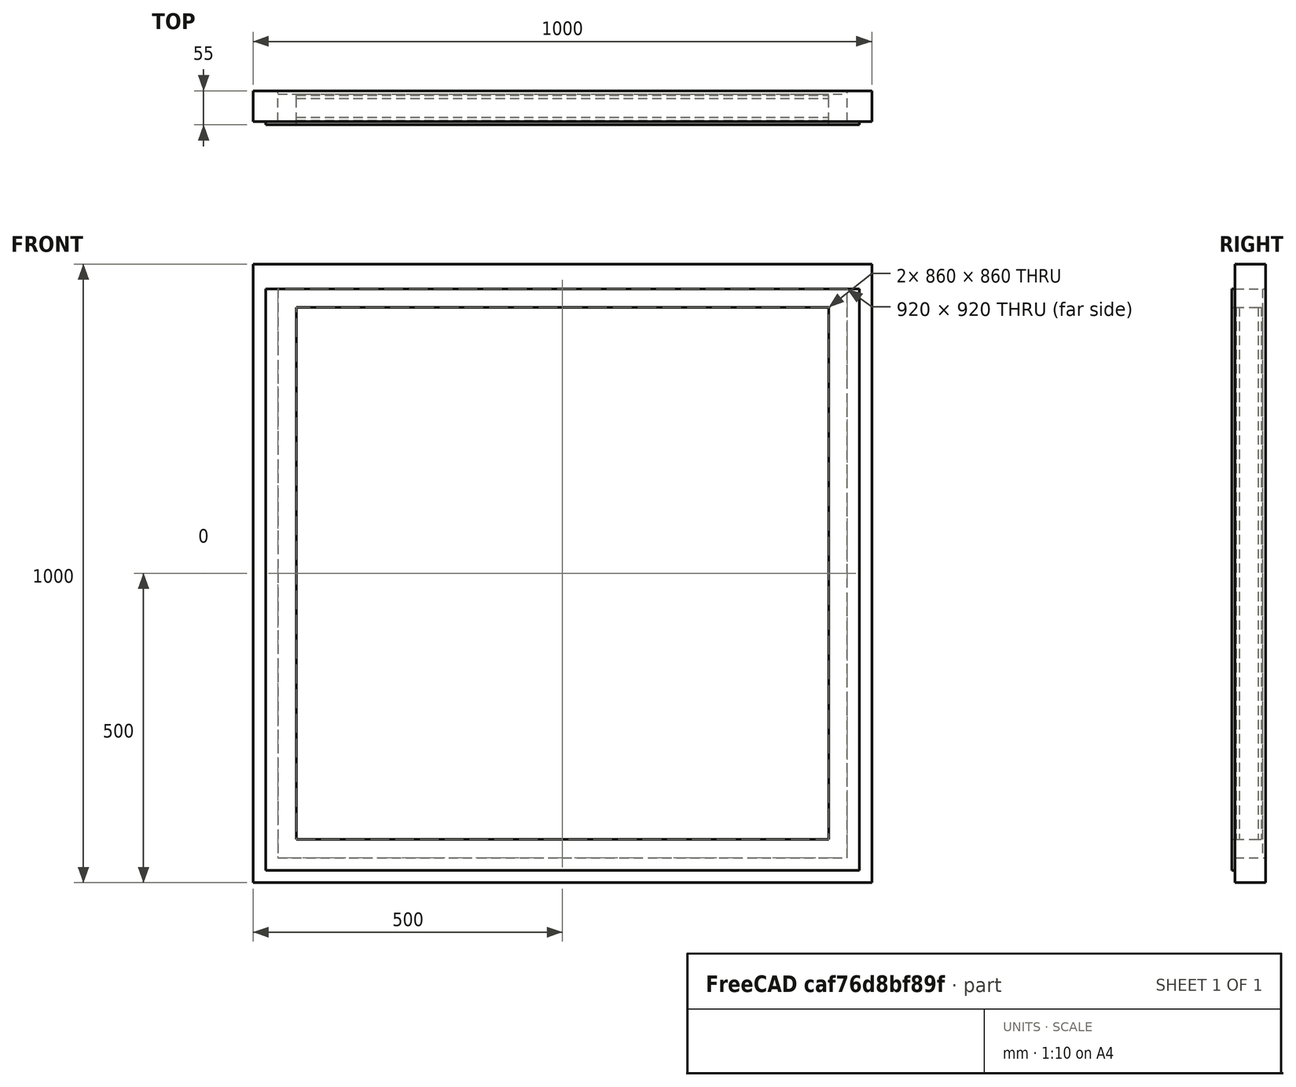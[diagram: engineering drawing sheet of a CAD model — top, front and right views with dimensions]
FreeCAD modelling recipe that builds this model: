
FCSTD DOCUMENT  (FreeCAD 0.16R6704 (Git))
Label: Maxim Air with double glazing and blind
License: CreativeCommons Attribution
LicenseURL: http://creativecommons.org/licenses/by/4.0/
objects: Sketcher::SketchObject×3, Part::FeaturePython×2, Part::Extrusion×1, App::DocumentObjectGroup×1
note: 6 computed .brp shape members not serialized (recipe doc carries the construction recipe); baked Part::Feature solids carry a one-line shape summary decoded from their .brp

FEATURE [Sketcher::SketchObject] Sketch102  label="Esboco_persiana_interna_02"
  Placement = pos=(0,0,0) rot=(1,0,0;1.5708rad)
  sketch-geometry (16):
    g0: LineSegment StartX=0 StartY=0 StartZ=0 EndX=1000 EndY=0 EndZ=0
    g1: LineSegment StartX=1000 StartY=0 StartZ=0 EndX=1000 EndY=1000 EndZ=0
    g2: LineSegment StartX=1000 StartY=1000 StartZ=0 EndX=0 EndY=1000 EndZ=0
    g3: LineSegment StartX=0 StartY=1000 StartZ=0 EndX=0 EndY=0 EndZ=0
    g4: LineSegment StartX=40 StartY=40 StartZ=0 EndX=960 EndY=40 EndZ=0
    g5: LineSegment StartX=960 StartY=40 StartZ=0 EndX=960 EndY=960 EndZ=0
    g6: LineSegment StartX=960 StartY=960 StartZ=0 EndX=40 EndY=960 EndZ=0
    g7: LineSegment StartX=40 StartY=960 StartZ=0 EndX=40 EndY=40 EndZ=0
    g8: LineSegment StartX=70 StartY=930 StartZ=0 EndX=930 EndY=930 EndZ=0
    g9: LineSegment StartX=930 StartY=930 StartZ=0 EndX=930 EndY=70 EndZ=0
    g10: LineSegment StartX=930 StartY=70 StartZ=0 EndX=70 EndY=70 EndZ=0
    g11: LineSegment StartX=70 StartY=70 StartZ=0 EndX=70 EndY=930 EndZ=0
    g12: LineSegment StartX=20 StartY=960 StartZ=0 EndX=980 EndY=960 EndZ=0
    g13: LineSegment StartX=980 StartY=960 StartZ=0 EndX=980 EndY=20 EndZ=0
    g14: LineSegment StartX=980 StartY=20 StartZ=0 EndX=20 EndY=20 EndZ=0
    g15: LineSegment StartX=20 StartY=20 StartZ=0 EndX=20 EndY=960 EndZ=0
  constraints (47):
    c: Coincident(g0,g1)
    c: Coincident(g1,g2)
    c: Coincident(g2,g3)
    c: Coincident(g3,g0)
    c: Horizontal(g0)
    c: Horizontal(g2)
    c: Vertical(g1)
    c: Vertical(g3)
    c: Coincident(g4,g5)
    c: Coincident(g5,g6)
    c: Coincident(g6,g7)
    c: Coincident(g7,g4)
    c: Horizontal(g4)
    c: Horizontal(g6)
    c: Vertical(g5)
    c: Vertical(g7)
    c: DistanceX(g0) = 1000  'Largura_vao'
    c: DistanceX(g2,g6) = 40  'Montante_vertical_1'
    c: DistanceX(g4,g0) = 40  'Montante_vertical_2'
    c: DistanceY(g0,g4) = 40  'Montante_inferior_caixilho'
    c: Coincident(g0,g-1)
    c: DistanceY(g0,g1) = 1000  'Altura_vao'
    c: Coincident(g8,g9)
    c: Coincident(g9,g10)
    c: Coincident(g10,g11)
    c: Coincident(g11,g8)
    c: Horizontal(g8)
    c: Horizontal(g10)
    c: Vertical(g9)
    c: Vertical(g11)
    c: DistanceX(g6,g8) = 30  'Montante_vertical_1_janela'
    c: DistanceY(g8,g6) = 30  'Montante_superior_janela'
    c: DistanceX(g8,g5) = 30  'Montante_vertical_2_janela'
    c: DistanceY(g4,g9) = 30  'Montante_inferior_janela'
    c: Coincident(g12,g13)
    c: Coincident(g13,g14)
    c: Coincident(g14,g15)
    c: Coincident(g15,g12)
    c: Horizontal(g12)
    c: Horizontal(g14)
    c: Vertical(g13)
    c: Vertical(g15)
    c: DistanceX(g4,g13) = 20  'Arremate vertical 2 janela'
    c: DistanceY(g13,g4) = 20  'Arremate_inferior'
    c: DistanceX(g14,g4) = 20  'Arremate_vertical_1'
    c: DistanceY(g6,g12) = 0
    c: DistanceY(g5,g1) = 40  'Montante_superior'
FEATURE [Part::FeaturePython] Window077  label="Maxim Air with double glazing and blind"  # WARN: FeaturePython — macro-defined, semantics opaque (R4)
  Base = -> Sketch102
  Height = 0
  HoleDepth = 0
  MoveWithHost = true
  Normal = (0,1,0)
  Preset = 0
  Role = 0
  Width = 0
  WindowParts = CAIXILHO | Frame | Wire0,Wire1 | 50.0 | 0.0 | JANELA | Frame | Wire1,Wire2 | 45.0 | 0.0 | ARREMATE | Frame | Wire2,Wire3 | 5.0 | -5.0 | VIDRO 1 | Glass panel | Wire2 | 5.0 | 2.0 | VIDRO 2 | Glass panel | Wire2 | 5.0 | 37.5
FEATURE [Sketcher::SketchObject] Sketch103
  ExternalGeometry = -> [Window077]
  Placement = pos=(70,0,0) rot=(0.57735,0.57735,0.57735;2.0944rad)
  Support = -> Window077 [Face19]
  sketch-geometry (3):
    g0: LineSegment [constr] StartX=22.5 StartY=1251.7 StartZ=0 EndX=22.5 EndY=-119.798 EndZ=0
    g1: ArcOfCircle CenterX=22.5 CenterY=921 CenterZ=0 NormalX=0 NormalY=0 NormalZ=1 Radius=7 StartAngle=1.5708 EndAngle=4.71239
    g2: ArcOfCircle CenterX=22.5 CenterY=907 CenterZ=0 NormalX=0 NormalY=0 NormalZ=1 Radius=7 StartAngle=4.71239 EndAngle=7.85398
  constraints (12):
    c: PointOnObject(g1,g0)
    c: PointOnObject(g1,g0)
    c: PointOnObject(g2,g0)
    c: PointOnObject(g2,g0)
    c: DistanceY(g1,g1) = 14
    c: DistanceY(g2,g1) = 14
    c: Vertical(g0)
    c: PointOnObject(g1,g0)
    c: PointOnObject(g2,g0)
    c: Coincident(g2,g1)
    c: Symmetric(g-3,g-3,g0)
    c: DistanceY(g1,g-3) = 2
FEATURE [Part::Extrusion] Extrude_Sketch103  label="Módulo persiana "
  Base = -> Sketch103
  Dir = (860,0,0)
  Solid = true
  expr: Dir.x = Esboco_persiana_interna_02.Constraints.Largura_vao - Esboco_persiana_interna_02.Constraints.Montante_vertical_1 - Esboco_persiana_interna_02.Constraints.Montante_vertical_1_janela - Esboco_persiana_interna_02.Constraints.Montante_vertical_2_janela - Esboco_persiana_interna_02.Constraints.Montante_vertical_2
FEATURE [Sketcher::SketchObject] Sketch104  label="Opening indication"
  ExternalGeometry = -> [Window077]
  Placement = pos=(0,2,0) rot=(1,0,0;1.5708rad)
  Support = -> Window077 [Face35]
  sketch-geometry (3):
    g0: LineSegment StartX=70 StartY=930 StartZ=0 EndX=500 EndY=70 EndZ=0
    g1: LineSegment StartX=500 StartY=70 StartZ=0 EndX=930 EndY=930 EndZ=0
    g2: LineSegment [constr] StartX=500 StartY=1142.4 StartZ=0 EndX=500 EndY=-164.202 EndZ=0
  constraints (7):
    c: Coincident(g-5,g0)
    c: PointOnObject(g0,g-4)
    c: Coincident(g0,g1)
    c: Vertical(g2)
    c: PointOnObject(g0,g2)
    c: Symmetric(g-5,g-6,g2)
    c: Coincident(g1,g-6)
FEATURE [Part::FeaturePython] Array004  label="Internal blind"  # Draft array (typed FeaturePython)
  Angle = 360
  ArrayType = 0
  Axis = (0,0,1)
  Base = -> Extrude_Sketch103
  Center = (0,0,0)
  Fuse = false
  IntervalAxis = (0,0,0)
  IntervalX = (1,0,0)
  IntervalY = (0,1,0)
  IntervalZ = (0,0,-28)
  NumberPolar = 1
  NumberX = 1
  NumberY = 1
  NumberZ = 31
  expr: NumberZ = (Esboco_persiana_interna_02.Constraints.Altura_vao - Esboco_persiana_interna_02.Constraints.Montante_inferior_caixilho - Esboco_persiana_interna_02.Constraints.Montante_inferior_janela - Esboco_persiana_interna_02.Constraints.Montante_superior_janela - Esboco_persiana_interna_02.Constraints.Montante_superior) / 28
FEATURE [App::DocumentObjectGroup] Grupo085  label="Maxim Air with double glazing and blind "
  Group = -> [Window077,Sketch104,Extrude_Sketch103,Array004]
